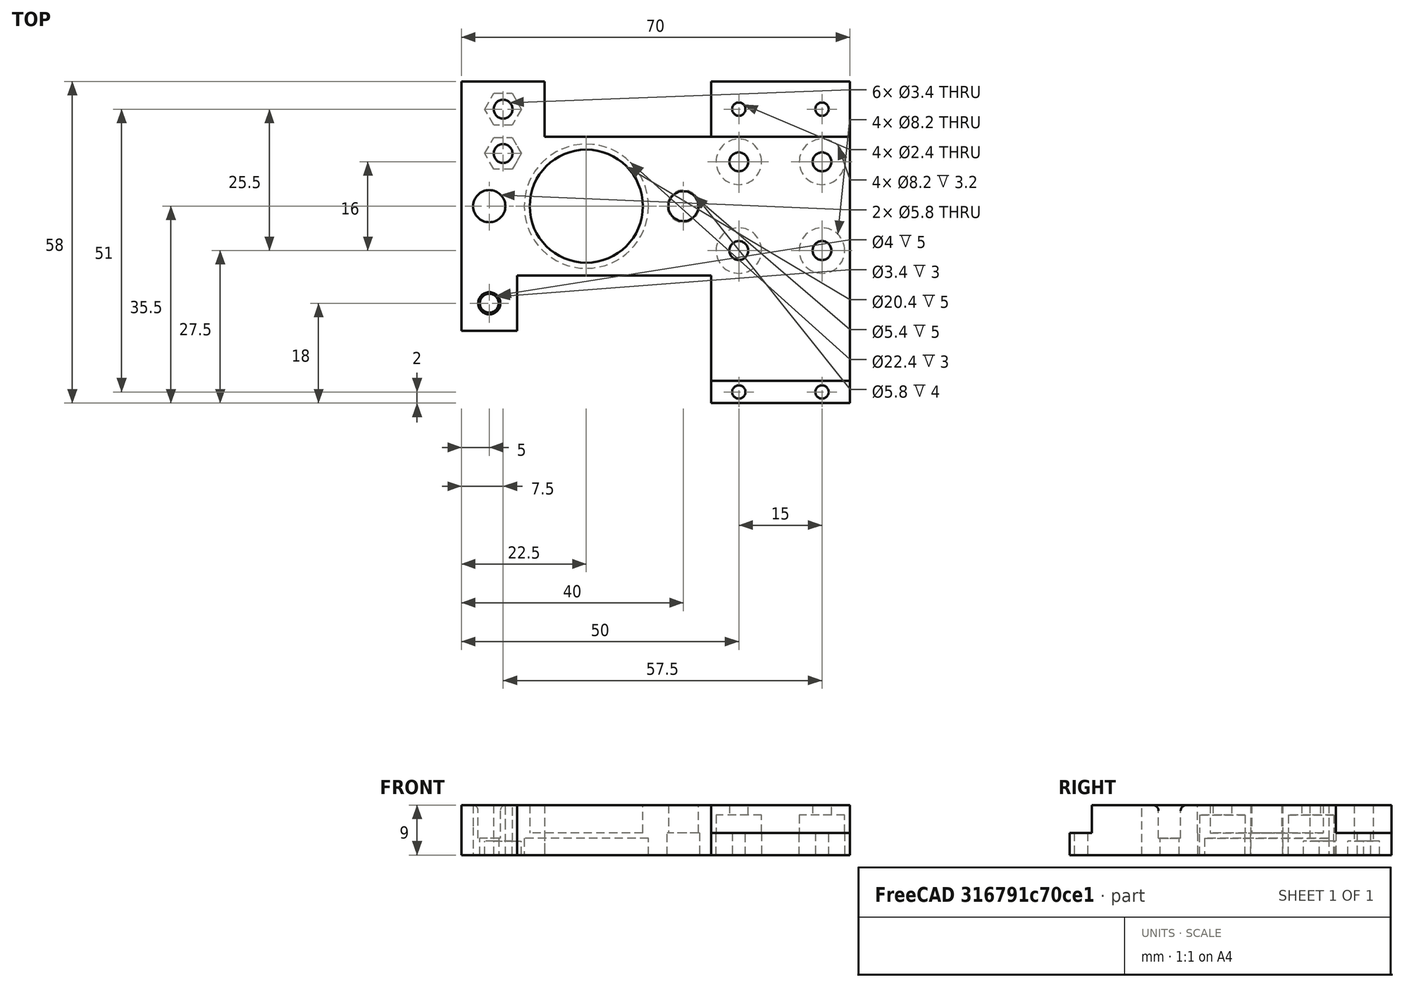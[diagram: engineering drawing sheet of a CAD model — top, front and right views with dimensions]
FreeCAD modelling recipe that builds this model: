
FCSTD DOCUMENT  (FreeCAD 0.18.4R)
Label: down_left_support_MGN9H
License: All rights reserved
LicenseURL: http://en.wikipedia.org/wiki/All_rights_reserved
objects: Sketcher::SketchObject×16, PartDesign::Pocket×9, PartDesign::Pad×7, Mesh::Feature×1, PartDesign::Fillet×1, PartDesign::Body×1
note: 50 computed .brp shape members not serialized (recipe doc carries the construction recipe); baked Part::Feature solids carry a one-line shape summary decoded from their .brp

FEATURE [Sketcher::SketchObject] Sketch
  MapMode = 5
  Support = -> [XY_Plane]
  sketch-geometry (10):
    g0: LineSegment StartX=-30 StartY=12.5 StartZ=0 EndX=30 EndY=12.5 EndZ=0
    g1: LineSegment StartX=30 StartY=12.5 StartZ=0 EndX=30 EndY=-12.5 EndZ=0
    g2: LineSegment StartX=30 StartY=-12.5 StartZ=0 EndX=-30 EndY=-12.5 EndZ=0
    g3: LineSegment StartX=-30 StartY=-12.5 StartZ=0 EndX=-30 EndY=12.5 EndZ=0
    g4: Circle CenterX=10 CenterY=8 CenterZ=0 NormalX=0 NormalY=0 NormalZ=1 AngleXU=0 Radius=1.7
    g5: Circle CenterX=25 CenterY=8 CenterZ=0 NormalX=0 NormalY=0 NormalZ=1 AngleXU=0 Radius=1.7
    g6: Circle CenterX=10 CenterY=-8 CenterZ=0 NormalX=0 NormalY=0 NormalZ=1 AngleXU=0 Radius=1.7
    g7: Circle CenterX=25 CenterY=-8 CenterZ=0 NormalX=0 NormalY=0 NormalZ=1 AngleXU=0 Radius=1.7
    g8: Circle CenterX=-17.5 CenterY=0 CenterZ=0 NormalX=0 NormalY=0 NormalZ=1 AngleXU=0 Radius=10.2
    g9: Circle CenterX=9e-16 CenterY=0 CenterZ=0 NormalX=0 NormalY=0 NormalZ=1 AngleXU=0 Radius=2.7
  constraints (26):
    c: Coincident(g0,g1)
    c: Coincident(g1,g2)
    c: Coincident(g2,g3)
    c: Coincident(g3,g0)
    c: Horizontal(g2)
    c: Vertical(g1)
    c: Symmetric(g0,g0,g-2)
    c: Symmetric(g0,g2,g-1)
    c: DistanceX(g0,g0) = 60
    c: DistanceY(g3,g3) = 25
    c: Symmetric(g7,g5,g-1)
    c: Symmetric(g4,g6,g-1)
    c: Distance(g6,g7) = 15
    c: Distance(g4,g6) = 16
    c: Horizontal(g5,g4)
    c: Radius(g4) = 1.7
    c: Radius(g5) = 1.7
    c: Radius(g7) = 1.7
    c: Radius(g6) = 1.7
    c: Distance(g5,g1) = 5
    c: Radius(g8) = 10.2
    c: PointOnObject(g8,g-1)
    c: Distance(g8,g3) = 12.5
    c: PointOnObject(g9,g-1)
    c: Distance(g9,g8) = 17.5
    c: Radius(g9) = 2.7
FEATURE [PartDesign::Pad] Pad
  Length = 5
  Length2 = 100
  Profile = -> Sketch
  Type = 0
FEATURE [Sketcher::SketchObject] Sketch001
  ExternalGeometry = -> [Pad]
  MapMode = 5
  Placement = pos=(0,0,0) rot=(1,0,0;3.14159rad)
  Support = -> [Pad]
  sketch-geometry (4):
    g0: Circle CenterX=25 CenterY=8 CenterZ=0 NormalX=0 NormalY=0 NormalZ=1 AngleXU=0 Radius=4.1
    g1: Circle CenterX=25 CenterY=-8 CenterZ=0 NormalX=0 NormalY=0 NormalZ=1 AngleXU=0 Radius=4.1
    g2: Circle CenterX=10 CenterY=8 CenterZ=0 NormalX=0 NormalY=0 NormalZ=1 AngleXU=0 Radius=4.1
    g3: Circle CenterX=10 CenterY=-8 CenterZ=0 NormalX=0 NormalY=0 NormalZ=1 AngleXU=0 Radius=4.1
  constraints (8):
    c: Coincident(g0,g-4)
    c: Coincident(g1,g-5)
    c: Coincident(g2,g-6)
    c: Radius(g0) = 4.1
    c: Radius(g1) = 4.1
    c: Radius(g2) = 4.1
    c: Coincident(g3,g-11)
    c: Radius(g3) = 4.1
FEATURE [PartDesign::Pocket] Pocket001
  BaseFeature = -> Pad
  Length = 3.2
  Length2 = 100
  Profile = -> Sketch001
  Type = 0
FEATURE [Sketcher::SketchObject] Sketch002
  ExternalGeometry = -> [Pocket001]
  MapMode = 5
  Placement = pos=(0,0,0) rot=(1,0,0;3.14159rad)
  Support = -> [Pocket001]
  sketch-geometry (9):
    g0: LineSegment StartX=-30 StartY=12.5 StartZ=0 EndX=30 EndY=12.5 EndZ=0
    g1: LineSegment StartX=30 StartY=12.5 StartZ=0 EndX=30 EndY=-12.5 EndZ=0
    g2: LineSegment StartX=30 StartY=-12.5 StartZ=0 EndX=-30 EndY=-12.5 EndZ=0
    g3: LineSegment StartX=-30 StartY=-12.5 StartZ=0 EndX=-30 EndY=12.5 EndZ=0
    g4: Circle CenterX=0 CenterY=0 CenterZ=0 NormalX=0 NormalY=0 NormalZ=1 AngleXU=0 Radius=2.9
    g5: Circle CenterX=10 CenterY=8 CenterZ=0 NormalX=0 NormalY=0 NormalZ=1 AngleXU=0 Radius=4.1
    g6: Circle CenterX=10 CenterY=-8 CenterZ=0 NormalX=0 NormalY=0 NormalZ=1 AngleXU=0 Radius=4.1
    g7: Circle CenterX=25 CenterY=8 CenterZ=0 NormalX=0 NormalY=0 NormalZ=1 AngleXU=0 Radius=4.1
    g8: Circle CenterX=25 CenterY=-8 CenterZ=0 NormalX=0 NormalY=0 NormalZ=1 AngleXU=0 Radius=4.1
  constraints (20):
    c: Coincident(g0,g1)
    c: Coincident(g1,g2)
    c: Coincident(g2,g3)
    c: Coincident(g3,g0)
    c: Horizontal(g0)
    c: Horizontal(g2)
    c: Vertical(g1)
    c: Vertical(g3)
    c: Coincident(g0,g-6)
    c: Coincident(g1,g-5)
    c: Coincident(g4,g-1)
    c: Coincident(g5,g-8)
    c: Coincident(g6,g-9)
    c: Coincident(g7,g-10)
    c: Coincident(g8,g-11)
    c: Radius(g4) = 2.9
    c: Radius(g5) = 4.1
    c: Radius(g7) = 4.1
    c: Radius(g8) = 4.1
    c: Radius(g6) = 4.1
FEATURE [PartDesign::Pad] Pad001
  BaseFeature = -> Pocket001
  Length = 4
  Length2 = 100
  Profile = -> Sketch002
  Type = 0
FEATURE [Sketcher::SketchObject] Sketch003
  ExternalGeometry = -> [Pad001]
  MapMode = 5
  Placement = pos=(0,0,-4) rot=(1,0,0;3.14159rad)
  Support = -> [Pad001]
  sketch-geometry (1):
    g0: Circle CenterX=-17.5 CenterY=0 CenterZ=0 NormalX=0 NormalY=0 NormalZ=1 AngleXU=0 Radius=11.2
  constraints (3):
    c: PointOnObject(g0,g-1)
    c: Radius(g0) = 11.2
    c: Distance(g0,g-4) = 12.5
FEATURE [PartDesign::Pocket] Pocket
  BaseFeature = -> Pad001
  Length = 3
  Length2 = 100
  Profile = -> Sketch003
  Type = 0
FEATURE [Sketcher::SketchObject] Sketch004
  ExternalGeometry = -> [Pocket]
  MapMode = 5
  Placement = pos=(-30,0,0) rot=(0.57735,-0.57735,-0.57735;2.0944rad)
  Support = -> [Pocket]
  sketch-geometry (4):
    g0: LineSegment StartX=12.5 StartY=-4 StartZ=0 EndX=-12.5 EndY=-4 EndZ=0
    g1: LineSegment StartX=-12.5 StartY=-4 StartZ=0 EndX=-12.5 EndY=5 EndZ=0
    g2: LineSegment StartX=-12.5 StartY=5 StartZ=0 EndX=12.5 EndY=5 EndZ=0
    g3: LineSegment StartX=12.5 StartY=5 StartZ=0 EndX=12.5 EndY=-4 EndZ=0
  constraints (12):
    c: Coincident(g0,g1)
    c: Coincident(g1,g2)
    c: Coincident(g2,g3)
    c: Coincident(g3,g0)
    c: Horizontal(g2)
    c: Vertical(g1)
    c: Vertical(g3)
    c: PointOnObject(g0,g-3)
    c: DistanceX(g0,g0) = 25
    c: Symmetric(g0,g0,g-2)
    c: PointOnObject(g1,g-4)
    c: Distance(g-3) = 25
FEATURE [PartDesign::Pad] Pad002
  BaseFeature = -> Pocket
  Length = 10
  Length2 = 100
  Profile = -> Sketch004
  Type = 0
FEATURE [Sketcher::SketchObject] Sketch005
  ExternalGeometry = -> [Pad002]
  MapMode = 5
  Placement = pos=(0,0,-4) rot=(1,0,0;3.14159rad)
  Support = -> [Pad002]
  sketch-geometry (1):
    g0: Circle CenterX=-35 CenterY=0 CenterZ=0 NormalX=0 NormalY=0 NormalZ=1 AngleXU=0 Radius=2.9
  constraints (3):
    c: PointOnObject(g0,g-1)
    c: Distance(g-3,g0) = 17.5
    c: Radius(g0) = 2.9
FEATURE [PartDesign::Pocket] Pocket002
  BaseFeature = -> Pad002
  Length = 5
  Length2 = 100
  Profile = -> Sketch005
  Type = 0
FEATURE [Mesh::Feature] belt_support_left001
  Placement = pos=(-15,-17,5) rot=(0,0,1;0rad)
FEATURE [Sketcher::SketchObject] Sketch006
  ExternalGeometry = -> [Pocket002]
  MapMode = 5
  Placement = pos=(0,-12.5,0) rot=(1,0,0;1.5708rad)
  Support = -> [Pocket002]
  sketch-geometry (4):
    g0: LineSegment StartX=30 StartY=-4 StartZ=0 EndX=5 EndY=-4 EndZ=0
    g1: LineSegment StartX=5 StartY=-4 StartZ=0 EndX=5 EndY=5 EndZ=0
    g2: LineSegment StartX=5 StartY=5 StartZ=0 EndX=30 EndY=5 EndZ=0
    g3: LineSegment StartX=30 StartY=5 StartZ=0 EndX=30 EndY=-4 EndZ=0
  constraints (11):
    c: Coincident(g0,g1)
    c: Coincident(g1,g2)
    c: Coincident(g2,g3)
    c: Coincident(g3,g0)
    c: Horizontal(g0)
    c: Horizontal(g2)
    c: Vertical(g1)
    c: Vertical(g3)
    c: Coincident(g0,g-4)
    c: Distance(g0) = 25
    c: PointOnObject(g1,g-3)
FEATURE [PartDesign::Pad] Pad003
  BaseFeature = -> Pocket002
  Length = 23
  Length2 = 100
  Profile = -> Sketch006
  Type = 0
FEATURE [Sketcher::SketchObject] Sketch007
  ExternalGeometry = -> [Pad003]
  MapMode = 5
  Placement = pos=(0,12.5,0) rot=(0,0.707107,0.707107;3.14159rad)
  Support = -> [Pad003]
  sketch-geometry (4):
    g0: LineSegment StartX=-30 StartY=-4 StartZ=0 EndX=-5 EndY=-4 EndZ=0
    g1: LineSegment StartX=-5 StartY=-4 StartZ=0 EndX=-5 EndY=0 EndZ=0
    g2: LineSegment StartX=-5 StartY=0 StartZ=0 EndX=-30 EndY=0 EndZ=0
    g3: LineSegment StartX=-30 StartY=0 StartZ=0 EndX=-30 EndY=-4 EndZ=0
  constraints (11):
    c: Coincident(g0,g1)
    c: Coincident(g1,g2)
    c: Coincident(g2,g3)
    c: Coincident(g3,g0)
    c: Horizontal(g0)
    c: Horizontal(g2)
    c: Vertical(g1)
    c: Vertical(g3)
    c: Coincident(g0,g-3)
    c: PointOnObject(g1,g-1)
    c: Distance(g0) = 25
FEATURE [PartDesign::Pad] Pad004
  BaseFeature = -> Pad003
  Length = 10
  Length2 = 100
  Profile = -> Sketch007
  Type = 0
FEATURE [Sketcher::SketchObject] Sketch008
  ExternalGeometry = -> [Pad004]
  MapMode = 5
  Placement = pos=(0,12.5,0) rot=(0,0.707107,0.707107;3.14159rad)
  Support = -> [Pad004]
  sketch-geometry (4):
    g0: LineSegment StartX=40 StartY=5 StartZ=0 EndX=25 EndY=5 EndZ=0
    g1: LineSegment StartX=25 StartY=5 StartZ=0 EndX=25 EndY=-4 EndZ=0
    g2: LineSegment StartX=25 StartY=-4 StartZ=0 EndX=40 EndY=-4 EndZ=0
    g3: LineSegment StartX=40 StartY=-4 StartZ=0 EndX=40 EndY=5 EndZ=0
  constraints (12):
    c: Coincident(g0,g1)
    c: Coincident(g1,g2)
    c: Coincident(g2,g3)
    c: Coincident(g3,g0)
    c: Horizontal(g0)
    c: Horizontal(g2)
    c: Vertical(g1)
    c: Vertical(g3)
    c: PointOnObject(g0,g-4)
    c: PointOnObject(g1,g-3)
    c: DistanceX(g2,g2) = 15
    c: PointOnObject(g0,g-5)
FEATURE [PartDesign::Pad] Pad005
  BaseFeature = -> Pad004
  Length = 10
  Length2 = 100
  Profile = -> Sketch008
  Type = 0
FEATURE [Sketcher::SketchObject] Sketch009
  ExternalGeometry = -> [Pad005]
  MapMode = 5
  Placement = pos=(0,1.1e-15,5) rot=(0,0,1;0rad)
  Support = -> [Pad005]
  sketch-geometry (4):
    g0: LineSegment StartX=5 StartY=-35.5 StartZ=0 EndX=30 EndY=-35.5 EndZ=0
    g1: LineSegment StartX=30 StartY=-35.5 StartZ=0 EndX=30 EndY=-31.5 EndZ=0
    g2: LineSegment StartX=30 StartY=-31.5 StartZ=0 EndX=5 EndY=-31.5 EndZ=0
    g3: LineSegment StartX=5 StartY=-31.5 StartZ=0 EndX=5 EndY=-35.5 EndZ=0
  constraints (11):
    c: Coincident(g0,g1)
    c: Coincident(g1,g2)
    c: Coincident(g2,g3)
    c: Coincident(g3,g0)
    c: Horizontal(g0)
    c: Horizontal(g2)
    c: Vertical(g1)
    c: Vertical(g3)
    c: Coincident(g0,g-5)
    c: PointOnObject(g1,g-4)
    c: DistanceY(g1,g1) = 4
FEATURE [PartDesign::Pocket] Pocket003
  BaseFeature = -> Pad005
  Length = 5
  Length2 = 100
  Profile = -> Sketch009
  Type = 0
FEATURE [Sketcher::SketchObject] Sketch010
  ExternalGeometry = -> [Pocket003]
  MapMode = 5
  Placement = pos=(0,-9e-16,-4) rot=(1,0,0;3.14159rad)
  Support = -> [Pocket003]
  sketch-geometry (6):
    g0: Circle CenterX=10 CenterY=33.5 CenterZ=0 NormalX=0 NormalY=0 NormalZ=1 AngleXU=0 Radius=1.2
    g1: Circle CenterX=25 CenterY=33.5 CenterZ=0 NormalX=0 NormalY=0 NormalZ=1 AngleXU=0 Radius=1.2
    g2: Circle CenterX=10 CenterY=-17.5 CenterZ=0 NormalX=0 NormalY=0 NormalZ=1 AngleXU=0 Radius=1.2
    g3: Circle CenterX=25 CenterY=-17.5 CenterZ=0 NormalX=0 NormalY=0 NormalZ=1 AngleXU=0 Radius=1.2
    g4: Circle CenterX=-32.5 CenterY=-9.5 CenterZ=0 NormalX=0 NormalY=0 NormalZ=1 AngleXU=0 Radius=1.7
    g5: Circle CenterX=-32.5 CenterY=-17.5 CenterZ=0 NormalX=0 NormalY=0 NormalZ=1 AngleXU=0 Radius=1.7
  constraints (19):
    c: Radius(g3) = 1.2
    c: Radius(g2) = 1.2
    c: Radius(g0) = 1.2
    c: Radius(g1) = 1.2
    c: Horizontal(g0,g1)
    c: Vertical(g0,g2)
    c: Horizontal(g2,g3)
    c: Vertical(g1,g3)
    c: Distance(g1,g0) = 15
    c: Distance(g2,g-5) = 5
    c: Distance(g0,g-4) = 5
    c: Distance(g0,g-3) = 2
    c: Distance(g-4) = 23
    c: Vertical(g4,g5)
    c: Distance(g4,g-6) = 7.5
    c: Radius(g4) = 1.7
    c: Radius(g5) = 1.7
    c: Distance(g5,g4) = 8
    c: Distance(g5,g-8) = 5
FEATURE [PartDesign::Pocket] Pocket004
  BaseFeature = -> Pocket003
  Length = 9
  Length2 = 100
  Profile = -> Sketch010
  Type = 0
FEATURE [Sketcher::SketchObject] Sketch011
  ExternalGeometry = -> [Pocket004]
  MapMode = 5
  Placement = pos=(0,-9e-16,-4) rot=(1,0,0;3.14159rad)
  Support = -> [Pocket004]
  sketch-geometry (14):
    g0: LineSegment StartX=-30.85 StartY=-20.3579 StartZ=0 EndX=-29.2 EndY=-17.5 EndZ=0
    g1: LineSegment StartX=-29.2 StartY=-17.5 StartZ=0 EndX=-30.85 EndY=-14.6421 EndZ=0
    g2: LineSegment StartX=-30.85 StartY=-14.6421 StartZ=0 EndX=-34.15 EndY=-14.6421 EndZ=0
    g3: LineSegment StartX=-34.15 StartY=-14.6421 StartZ=0 EndX=-35.8 EndY=-17.5 EndZ=0
    g4: LineSegment StartX=-35.8 StartY=-17.5 StartZ=0 EndX=-34.15 EndY=-20.3579 EndZ=0
    g5: LineSegment StartX=-34.15 StartY=-20.3579 StartZ=0 EndX=-30.85 EndY=-20.3579 EndZ=0
    g6: Circle [constr] CenterX=-32.5 CenterY=-17.5 CenterZ=0 NormalX=0 NormalY=0 NormalZ=1 AngleXU=0 Radius=3.3
    g7: LineSegment StartX=-34.15 StartY=-12.3579 StartZ=0 EndX=-30.85 EndY=-12.3579 EndZ=0
    g8: LineSegment StartX=-30.85 StartY=-12.3579 StartZ=0 EndX=-29.2 EndY=-9.5 EndZ=0
    g9: LineSegment StartX=-29.2 StartY=-9.5 StartZ=0 EndX=-30.85 EndY=-6.64212 EndZ=0
    g10: LineSegment StartX=-30.85 StartY=-6.64212 StartZ=0 EndX=-34.15 EndY=-6.64212 EndZ=0
    g11: LineSegment StartX=-34.15 StartY=-6.64212 StartZ=0 EndX=-35.8 EndY=-9.5 EndZ=0
    g12: LineSegment StartX=-35.8 StartY=-9.5 StartZ=0 EndX=-34.15 EndY=-12.3579 EndZ=0
    g13: Circle [constr] CenterX=-32.5 CenterY=-9.5 CenterZ=0 NormalX=0 NormalY=0 NormalZ=1 AngleXU=0 Radius=3.3
  constraints (32):
    c: Coincident(g0,g1)
    c: Coincident(g1,g2)
    c: Coincident(g2,g3)
    c: Coincident(g3,g4)
    c: Coincident(g4,g5)
    c: Coincident(g5,g0)
    c: Equal(g0, g1-g5) x5
    c: PointOnObject(g0,g6)
    c: PointOnObject(g1,g6)
    c: PointOnObject(g2,g6)
    c: PointOnObject(g3,g6)
    c: PointOnObject(g4,g6)
    c: PointOnObject(g5,g6)
    c: Coincident(g6,g-4)
    c: Radius(g6) = 3.3
    c: Coincident(g7,g8)
    c: Coincident(g8,g9)
    c: Coincident(g9,g10)
    c: Coincident(g10,g11)
    c: Coincident(g11,g12)
    c: Coincident(g12,g7)
    c: Equal(g7, g8-g12) x5
    c: PointOnObject(g7,g13)
    c: PointOnObject(g8,g13)
    c: PointOnObject(g9,g13)
    c: PointOnObject(g10,g13)
    c: PointOnObject(g11,g13)
    c: PointOnObject(g12,g13)
    c: Coincident(g13,g-3)
    c: Parallel(g7,g2)
    c: Vertical(g2,g7)
    c: Radius(g13) = 3.3
FEATURE [PartDesign::Pocket] Pocket005
  BaseFeature = -> Pocket004
  Length = 2.5
  Length2 = 100
  Profile = -> Sketch011
  Type = 0
FEATURE [Sketcher::SketchObject] Sketch012
  ExternalGeometry = -> [Pocket005]
  MapMode = 5
  Placement = pos=(0,0,1) rot=(1,0,0;3.14159rad)
  Support = -> [Pocket005]
  sketch-geometry (1):
    g0: Circle CenterX=-35 CenterY=0 CenterZ=0 NormalX=0 NormalY=0 NormalZ=1 AngleXU=0 Radius=2.9
  constraints (2):
    c: Coincident(g0,g-3)
    c: Radius(g0) = 2.9
FEATURE [PartDesign::Pocket] Pocket006
  BaseFeature = -> Pocket005
  Length = 5
  Length2 = 100
  Profile = -> Sketch012
  Type = 0
FEATURE [Sketcher::SketchObject] Sketch013
  ExternalGeometry = -> [Pocket006]
  MapMode = 5
  Placement = pos=(0,-12.5,0) rot=(1,0,0;1.5708rad)
  Support = -> [Pocket006]
  sketch-geometry (4):
    g0: LineSegment StartX=-40 StartY=-4 StartZ=0 EndX=-30 EndY=-4 EndZ=0
    g1: LineSegment StartX=-30 StartY=-4 StartZ=0 EndX=-30 EndY=5 EndZ=0
    g2: LineSegment StartX=-30 StartY=5 StartZ=0 EndX=-40 EndY=5 EndZ=0
    g3: LineSegment StartX=-40 StartY=5 StartZ=0 EndX=-40 EndY=-4 EndZ=0
  constraints (10):
    c: Coincident(g0,g1)
    c: Coincident(g1,g2)
    c: Coincident(g2,g3)
    c: Coincident(g3,g0)
    c: Horizontal(g0)
    c: Horizontal(g2)
    c: Vertical(g1)
    c: Vertical(g3)
    c: Coincident(g0,g-4)
    c: Coincident(g1,g-5)
FEATURE [PartDesign::Pad] Pad006
  BaseFeature = -> Pocket006
  Length = 10
  Length2 = 100
  Profile = -> Sketch013
  Type = 0
FEATURE [Sketcher::SketchObject] Sketch014
  ExternalGeometry = -> [Pad006]
  MapMode = 5
  Placement = pos=(0,1.1e-15,5) rot=(0,0,1;0rad)
  Support = -> [Pad006]
  sketch-geometry (1):
    g0: Circle CenterX=-35 CenterY=-17.5 CenterZ=0 NormalX=0 NormalY=0 NormalZ=1 AngleXU=0 Radius=1.7
  constraints (5):
    c: Distance(g-4) = 10
    c: Distance(g-3) = 10
    c: Distance(g0,g-3) = 5
    c: Distance(g0,g-4) = 5
    c: Radius(g0) = 1.7
FEATURE [PartDesign::Pocket] Pocket007
  BaseFeature = -> Pad006
  Length = 9
  Length2 = 100
  Profile = -> Sketch014
  Type = 0
FEATURE [Sketcher::SketchObject] Sketch015
  ExternalGeometry = -> [Pocket007]
  MapMode = 5
  Placement = pos=(0,1.1e-15,5) rot=(0,0,1;0rad)
  Support = -> [Pocket007]
  sketch-geometry (1):
    g0: Circle CenterX=-35 CenterY=-17.5 CenterZ=0 NormalX=0 NormalY=0 NormalZ=1 AngleXU=0 Radius=2
  constraints (2):
    c: Coincident(g0,g-3)
    c: Radius(g0) = 2
FEATURE [PartDesign::Pocket] Pocket008
  BaseFeature = -> Pocket007
  Length = 6
  Length2 = 100
  Profile = -> Sketch015
  Type = 0
FEATURE [PartDesign::Fillet] Fillet
  Base = -> Pocket008 [Edge144]
  BaseFeature = -> Pocket008
  Radius = 1
FEATURE [PartDesign::Body] Body
  Group = -> [Sketch,Pad,Sketch001,Pocket001,Sketch002,Pad001,Sketch003,Pocket,Sketch004,Pad002,Sketch005,Pocket002,Sketch006,Pad003,Sketch007,Pad004,Sketch008,Pad005,Sketch009,Pocket003,Sketch010,Pocket004,Sketch011,Pocket005,Sketch012,Pocket006,Sketch013,Pad006,Sketch014,Pocket007,Sketch015,Pocket008,Fillet]
  Origin = -> Origin
  Tip = -> Fillet
